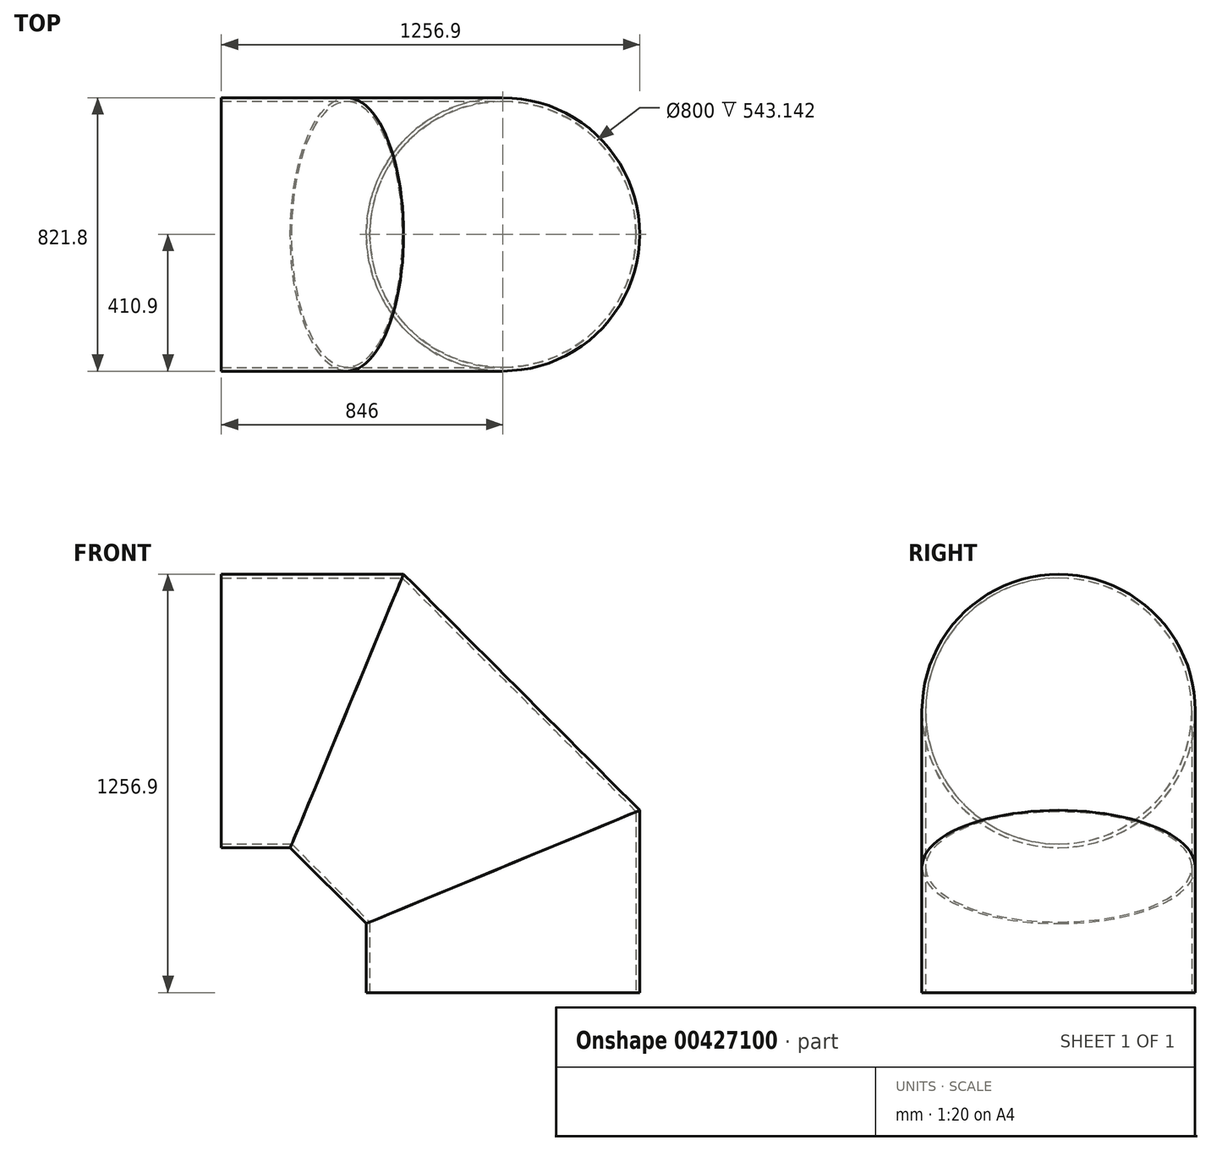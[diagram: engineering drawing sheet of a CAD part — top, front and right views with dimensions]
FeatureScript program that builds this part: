
annotation { "Feature Type Name" : "Feature", "Feature Type Description" : "" }
export const myFeature = defineFeature(function(context is Context, id is Id, definition is map)
    precondition{}
    {
        {
            var Q0;
            Q0=qCreatedBy(makeId("Front.planeOp"),FACE);
            var sketch = newSketch(context, id + "F0", { "sketchPlane" : qUnion([Q0])});
            skLineSegment(sketch, "E0", {"start": v(-46, 800) * mm, "end": v(331.37, 800) * mm});
            skLineSegment(sketch, "E1", {"start": v(331.37, 800) * mm, "end": v(800, 331.37) * mm});
            skLineSegment(sketch, "E2", {"start": v(800, -46) * mm, "end": v(800, 331.37) * mm});
            skCircle(sketch, "E3", {"center": v(0, 0) * mm, "radius": 800 * mm});
            skLineSegment(sketch, "E4", {"start": v(800, -331.37) * mm, "end": v(389.1, -331.37) * mm});
            skLineSegment(sketch, "E5", {"start": v(389.1, -331.37) * mm, "end": v(389.1, 162) * mm});
            skLineSegment(sketch, "E6", {"start": v(389.1, 162) * mm, "end": v(162, 389.1) * mm});
            skLineSegment(sketch, "E7", {"start": v(162, 389.1) * mm, "end": v(-331.37, 389.1) * mm});
            skLineSegment(sketch, "E8", {"start": v(-331.37, 389.1) * mm, "end": v(-331.37, 800) * mm});
            skLineSegment(sketch, "E9", {"start": v(-52.6, 0) * mm, "end": v(800, 0) * mm, "construction": true});
            skLineSegment(sketch, "E10", {"start": v(0, 0) * mm, "end": v(0, 800) * mm, "construction": true});
            skLineSegment(sketch, "E11", {"start": v(0, 0) * mm, "end": v(565.69, 565.69) * mm, "construction": true});
            skLineSegment(sketch, "E12", {"start": v(389.1, 64) * mm, "end": v(644.04, 64) * mm, "construction": true});
            skSolve(sketch);
        }
        {
            var Q0;
            Q0=sQuery(id+"F0.wireOp",VERTEX,"E0.start");
            var Q1;
            Q1=sQuery(id+"F0.wireOp",EDGE,"E0");
            cPlane(context, id + "F1", {"entities" : qUnion([Q0, Q1]), "cplaneType" : CPlaneType.LINE_POINT, "offset" : 0 * mm, "oppositeDirection" : true, "width" : 150 * mm, "height" : 150 * mm});
        }
        {
            var Q0;
            Q0=qCreatedBy(id+"F1.planeOp",FACE);
            var sketch = newSketch(context, id + "F2", { "sketchPlane" : qUnion([Q0])});
            skCircle(sketch, "E13", {"center": v(0, 800) * mm, "radius": 410.9 * mm});
            skCircle(sketch, "E14", {"center": v(0, 800) * mm, "radius": 400 * mm});
            skSolve(sketch);
        }
        {
            var Q0;
            Q0=makeQuery(id+"F2.imprint","IMPRINT",FACE,{"disambiguationData":[TD([[makeQuery(id+"F2.imprint","IMPRINT",EDGE,{"derivedFrom":sQuery(id+"F2.wireOp",EDGE,"E13")}),1.0]])]});
            var Q1;
            Q1=sQuery(id+"F2.wireOp",EDGE,"E13");
            var Q2;
            Q2=sQuery(id+"F0.wireOp",EDGE,"E0");
            var Q3;
            Q3=sQuery(id+"F0.wireOp",EDGE,"E1");
            var Q4;
            Q4=sQuery(id+"F0.wireOp",EDGE,"E2");
            sweep(context, id + "F3", {"profiles" : qUnion([Q0]), "surfaceProfiles" : qUnion([Q1]), "path" : qUnion([Q2, Q3, Q4])});
        }
    });
